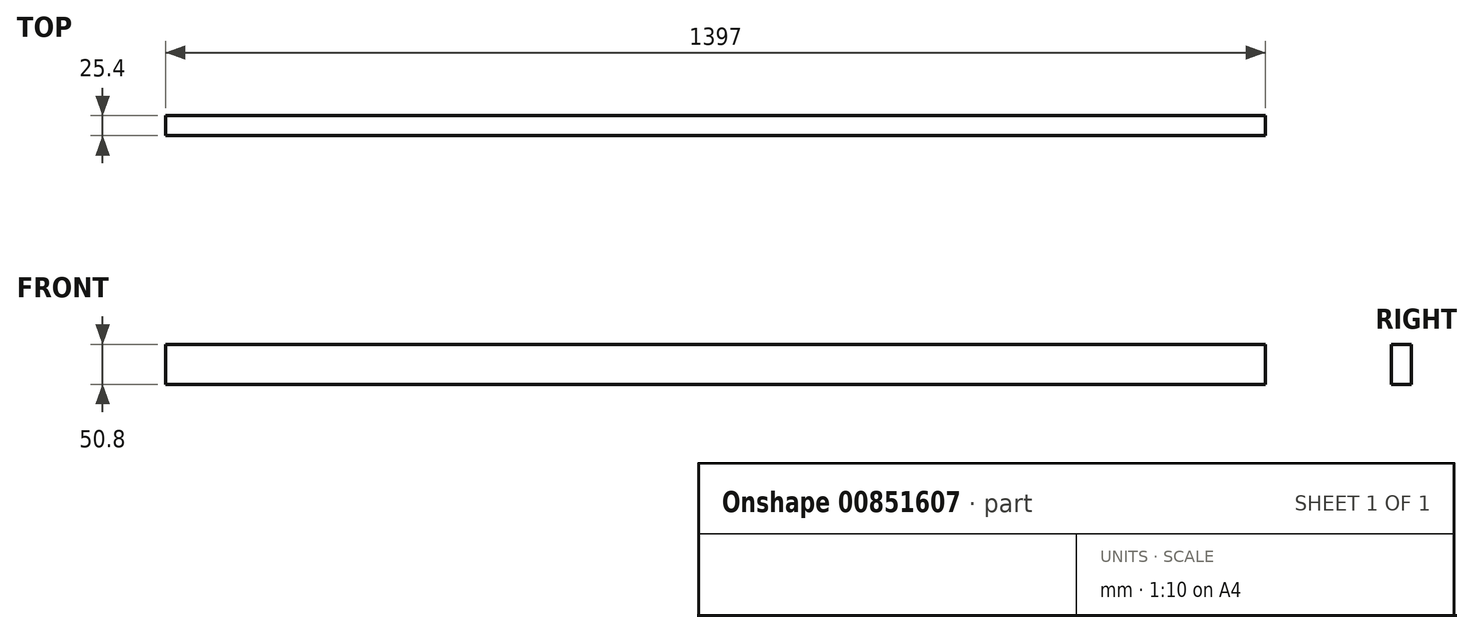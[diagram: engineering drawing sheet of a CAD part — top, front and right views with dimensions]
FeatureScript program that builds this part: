
annotation { "Feature Type Name" : "Feature", "Feature Type Description" : "" }
export const myFeature = defineFeature(function(context is Context, id is Id, definition is map)
    precondition{}
    {
        {
            var Q0;
            Q0=qCreatedBy(makeId("Front.planeOp"),FACE);
            var sketch = newSketch(context, id + "F0", { "sketchPlane" : qUnion([Q0])});
            skLineSegment(sketch, "E0.bottom", {"start": v(-701.17, -96.14) * mm, "end": v(695.83, -96.14) * mm});
            skLineSegment(sketch, "E0.top", {"start": v(-701.17, -146.94) * mm, "end": v(695.83, -146.94) * mm});
            skLineSegment(sketch, "E0.left", {"start": v(-701.17, -96.14) * mm, "end": v(-701.17, -146.94) * mm});
            skLineSegment(sketch, "E0.right", {"start": v(695.83, -96.14) * mm, "end": v(695.83, -146.94) * mm});
            skSolve(sketch);
        }
        {
            var Q0;
            Q0 = qSketchRegion(id + "F0", true);
            extrude(context, id + "F1", {"entities" : qUnion([Q0]), "depth" : 25.4 * mm, "offsetDistance" : 25.4 * mm});
        }
    });
